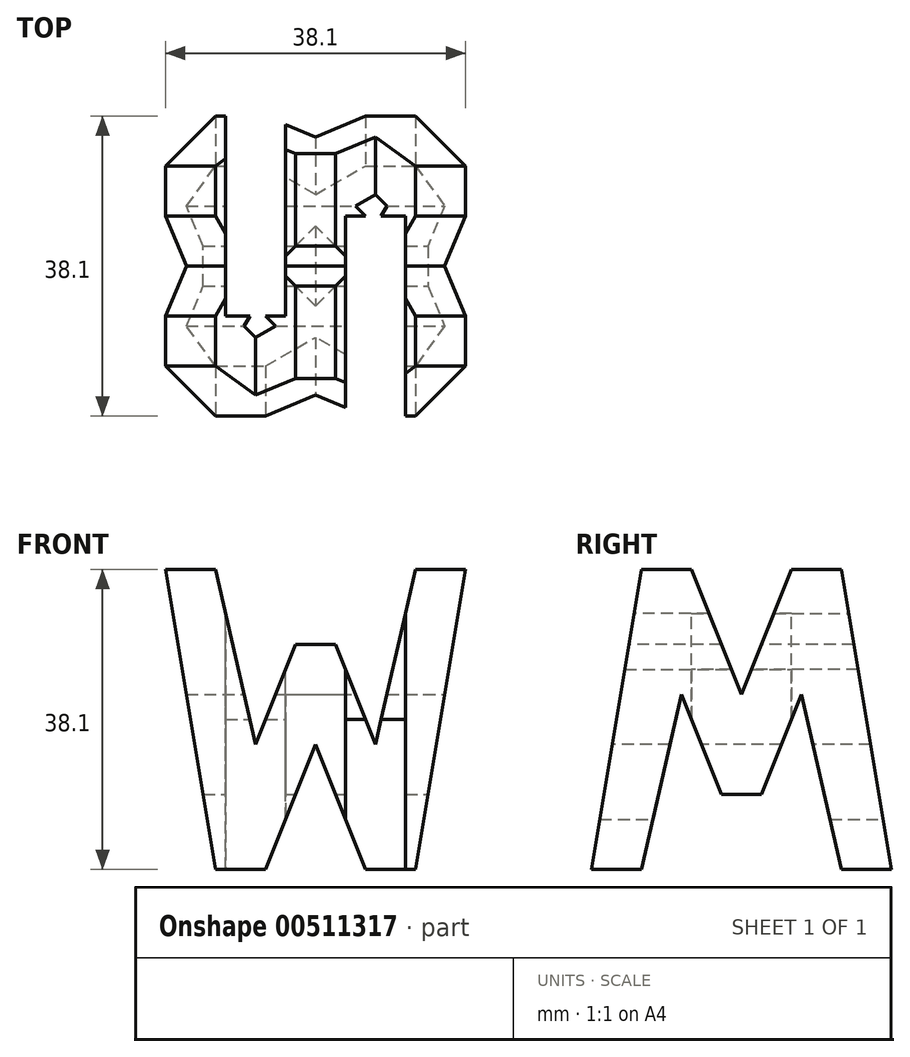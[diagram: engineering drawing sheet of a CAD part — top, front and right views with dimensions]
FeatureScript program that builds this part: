
annotation { "Feature Type Name" : "Feature", "Feature Type Description" : "" }
export const myFeature = defineFeature(function(context is Context, id is Id, definition is map)
    precondition{}
    {
        {
            var Q0;
            Q0=qCreatedBy(makeId("Front.planeOp"),FACE);
            var sketch = newSketch(context, id + "F0", { "sketchPlane" : qUnion([Q0])});
            skLineSegment(sketch, "E0", {"start": v(0, 0) * mm, "end": v(0, 38.1) * mm});
            skLineSegment(sketch, "E1", {"start": v(0, 38.1) * mm, "end": v(38.1, 38.1) * mm});
            skLineSegment(sketch, "E2", {"start": v(38.1, 38.1) * mm, "end": v(38.1, 0) * mm});
            skLineSegment(sketch, "E3", {"start": v(38.1, 0) * mm, "end": v(0, 0) * mm});
            skSolve(sketch);
        }
        {
            var Q0;
            Q0=makeQuery(id+"F0.imprint","IMPRINT",FACE,{"disambiguationData":[TD([[makeQuery(id+"F0.imprint","IMPRINT",EDGE,{"derivedFrom":sQuery(id+"F0.wireOp",EDGE,"E0")}),-1.0]])]});
            extrude(context, id + "F1", {"entities" : qUnion([Q0]), "depth" : 38.1 * mm, "offsetDistance" : 25.4 * mm});
        }
        {
            var Q0;
            Q0=qCreatedBy(makeId("Front.planeOp"),FACE);
            var Q1;
            Q1 = qBodyType(qCreatedBy(id + "F5" ,EDGE), BodyType.WIRE);
            cPlane(context, id + "F2", {"entities" : qUnion([Q0, Q1]), "cplaneType" : CPlaneType.OFFSET, "offset" : 38.1 * mm, "width" : 152.4 * mm, "height" : 152.4 * mm});
        }
        {
            var Q0;
            Q0=qCreatedBy(makeId("Right.planeOp"),FACE);
            cPlane(context, id + "F3", {"entities" : qUnion([Q0]), "cplaneType" : CPlaneType.OFFSET, "offset" : 38.1 * mm, "width" : 152.4 * mm, "height" : 152.4 * mm});
        }
        {
            var Q0;
            Q0=qCreatedBy(makeId("Top.planeOp"),FACE);
            cPlane(context, id + "F4", {"entities" : qUnion([Q0]), "cplaneType" : CPlaneType.OFFSET, "offset" : 38.1 * mm, "width" : 152.4 * mm, "height" : 152.4 * mm});
        }
        {
            var Q0;
            Q0=qCreatedBy(id+"F2.planeOp",FACE);
            var sketch = newSketch(context, id + "F5", { "sketchPlane" : qUnion([Q0])});
            skLineSegment(sketch, "E4.bottom", {"start": v(0, 0) * mm, "end": v(38.1, 0) * mm});
            skLineSegment(sketch, "E4.top", {"start": v(0, 38.1) * mm, "end": v(38.1, 38.1) * mm});
            skLineSegment(sketch, "E4.left", {"start": v(0, 0) * mm, "end": v(0, 38.1) * mm});
            skLineSegment(sketch, "E4.right", {"start": v(38.1, 0) * mm, "end": v(38.1, 38.1) * mm});
            skLineSegment(sketch, "E5", {"start": v(0, 38.1) * mm, "end": v(6.35, 0) * mm});
            skLineSegment(sketch, "E6", {"start": v(19.05, 15.87) * mm, "end": v(12.7, 0) * mm});
            skLineSegment(sketch, "E7", {"start": v(19.05, 15.87) * mm, "end": v(25.4, 0) * mm});
            skLineSegment(sketch, "E8", {"start": v(31.75, 0) * mm, "end": v(38.1, 38.1) * mm});
            skLineSegment(sketch, "E9", {"start": v(6.35, 38.1) * mm, "end": v(11.43, 15.87) * mm});
            skLineSegment(sketch, "E10", {"start": v(11.43, 15.87) * mm, "end": v(16.51, 28.57) * mm});
            skLineSegment(sketch, "E11", {"start": v(16.51, 28.57) * mm, "end": v(21.6, 28.57) * mm});
            skLineSegment(sketch, "E12", {"start": v(21.6, 28.57) * mm, "end": v(26.67, 15.87) * mm});
            skLineSegment(sketch, "E13", {"start": v(26.67, 15.87) * mm, "end": v(31.75, 38.1) * mm});
            skSolve(sketch);
        }
        {
            var Q0;
            {var subQ0=sQuery(id+"F5.wireOp",EDGE,"E6");Q0=makeQuery(id+"F5.imprint","IMPRINT",FACE,{"disambiguationData":[TD([[makeQuery(id+"F5.imprint","IMPRINT",EDGE,{"derivedFrom":subQ0}),1.0]])]});}
            var Q1;
            {var subQ0=sQuery(id+"F5.wireOp",EDGE,"E4.left");Q1=makeQuery(id+"F5.imprint","IMPRINT",FACE,{"disambiguationData":[TD([[makeQuery(id+"F5.imprint","IMPRINT",EDGE,{"derivedFrom":subQ0}),-1.0]])]});}
            var Q2;
            {var subQ0=sQuery(id+"F5.wireOp",EDGE,"E4.right");Q2=makeQuery(id+"F5.imprint","IMPRINT",FACE,{"disambiguationData":[TD([[makeQuery(id+"F5.imprint","IMPRINT",EDGE,{"derivedFrom":subQ0}),1.0]])]});}
            var Q3;
            {var subQ0=sQuery(id+"F5.wireOp",EDGE,"E9");Q3=makeQuery(id+"F5.imprint","IMPRINT",FACE,{"disambiguationData":[TD([[makeQuery(id+"F5.imprint","IMPRINT",EDGE,{"derivedFrom":subQ0}),1.0]])]});}
            extrude(context, id + "F6", {"entities" : qUnion([Q0, Q1, Q2, Q3]), "operationType" : NewBodyOperationType.REMOVE, "oppositeDirection" : true, "depth" : 38.1 * mm, "offsetDistance" : 25.4 * mm});
        }
        {
            var Q0;
            Q0=qCreatedBy(id+"F3.planeOp",FACE);
            var sketch = newSketch(context, id + "F7", { "sketchPlane" : qUnion([Q0])});
            skLineSegment(sketch, "E14", {"start": v(-31.75, 38.1) * mm, "end": v(-38.1, 0) * mm});
            skLineSegment(sketch, "E15", {"start": v(-25.4, 38.1) * mm, "end": v(-19.05, 22.23) * mm});
            skLineSegment(sketch, "E16", {"start": v(-19.05, 22.22) * mm, "end": v(-12.7, 38.1) * mm});
            skLineSegment(sketch, "E17", {"start": v(-6.35, 38.1) * mm, "end": v(0, 0) * mm});
            skLineSegment(sketch, "E18", {"start": v(-6.35, 0) * mm, "end": v(-11.43, 22.23) * mm});
            skLineSegment(sketch, "E19", {"start": v(-11.43, 22.23) * mm, "end": v(-16.5, 9.53) * mm});
            skLineSegment(sketch, "E20", {"start": v(-16.5, 9.53) * mm, "end": v(-21.59, 9.53) * mm});
            skLineSegment(sketch, "E21", {"start": v(-21.59, 9.52) * mm, "end": v(-26.67, 22.23) * mm});
            skLineSegment(sketch, "E22", {"start": v(-26.67, 22.23) * mm, "end": v(-31.75, 0) * mm});
            skLineSegment(sketch, "E23.bottom", {"start": v(-38.1, 0) * mm, "end": v(0, 0) * mm});
            skLineSegment(sketch, "E23.top", {"start": v(-38.1, 38.1) * mm, "end": v(0, 38.1) * mm});
            skLineSegment(sketch, "E23.left", {"start": v(-38.1, 0) * mm, "end": v(-38.1, 38.1) * mm});
            skLineSegment(sketch, "E23.right", {"start": v(0, 0) * mm, "end": v(0, 38.1) * mm});
            skSolve(sketch);
        }
        {
            var Q0;
            {var subQ0=sQuery(id+"F7.wireOp",EDGE,"E14");Q0=makeQuery(id+"F7.imprint","IMPRINT",FACE,{"disambiguationData":[TD([[makeQuery(id+"F7.imprint","IMPRINT",EDGE,{"derivedFrom":subQ0}),-1.0]])]});}
            var Q1;
            {var subQ0=sQuery(id+"F7.wireOp",EDGE,"E15");Q1=makeQuery(id+"F7.imprint","IMPRINT",FACE,{"disambiguationData":[TD([[makeQuery(id+"F7.imprint","IMPRINT",EDGE,{"derivedFrom":subQ0}),1.0]])]});}
            var Q2;
            {var subQ0=sQuery(id+"F7.wireOp",EDGE,"E17");Q2=makeQuery(id+"F7.imprint","IMPRINT",FACE,{"disambiguationData":[TD([[makeQuery(id+"F7.imprint","IMPRINT",EDGE,{"derivedFrom":subQ0}),1.0]])]});}
            var Q3;
            {var subQ0=sQuery(id+"F7.wireOp",EDGE,"E18");Q3=makeQuery(id+"F7.imprint","IMPRINT",FACE,{"disambiguationData":[TD([[makeQuery(id+"F7.imprint","IMPRINT",EDGE,{"derivedFrom":subQ0}),1.0]])]});}
            extrude(context, id + "F8", {"entities" : qUnion([Q0, Q1, Q2, Q3]), "operationType" : NewBodyOperationType.REMOVE, "oppositeDirection" : true, "depth" : 38.1 * mm, "offsetDistance" : 25.4 * mm});
        }
        {
            var Q0;
            Q0=qCreatedBy(id+"F4.planeOp",FACE);
            var sketch = newSketch(context, id + "F9", { "sketchPlane" : qUnion([Q0])});
            skLineSegment(sketch, "E24.bottom", {"start": v(0, -38.1) * mm, "end": v(38.1, -38.1) * mm});
            skLineSegment(sketch, "E24.top", {"start": v(0, 0) * mm, "end": v(38.1, 0) * mm});
            skLineSegment(sketch, "E24.left", {"start": v(0, -38.1) * mm, "end": v(0, 0) * mm});
            skLineSegment(sketch, "E24.right", {"start": v(38.1, -38.1) * mm, "end": v(38.1, 0) * mm});
            skLineSegment(sketch, "E25", {"start": v(7.62, 0) * mm, "end": v(7.62, -25.4) * mm});
            skLineSegment(sketch, "E26", {"start": v(7.62, -25.4) * mm, "end": v(15.24, -25.4) * mm});
            skLineSegment(sketch, "E27", {"start": v(15.24, -25.4) * mm, "end": v(15.24, 0) * mm});
            skLineSegment(sketch, "E28", {"start": v(30.48, -38.1) * mm, "end": v(30.48, -12.7) * mm});
            skLineSegment(sketch, "E29", {"start": v(30.48, -12.7) * mm, "end": v(22.86, -12.7) * mm});
            skLineSegment(sketch, "E30", {"start": v(22.86, -12.7) * mm, "end": v(22.86, -38.1) * mm});
            skSolve(sketch);
        }
        {
            var Q0;
            {var subQ0=sQuery(id+"F9.wireOp",EDGE,"E25");Q0=makeQuery(id+"F9.imprint","IMPRINT",FACE,{"disambiguationData":[TD([[makeQuery(id+"F9.imprint","IMPRINT",EDGE,{"derivedFrom":subQ0}),1.0]])]});}
            var Q1;
            {var subQ0=sQuery(id+"F9.wireOp",EDGE,"E28");Q1=makeQuery(id+"F9.imprint","IMPRINT",FACE,{"disambiguationData":[TD([[makeQuery(id+"F9.imprint","IMPRINT",EDGE,{"derivedFrom":subQ0}),1.0]])]});}
            extrude(context, id + "F10", {"entities" : qUnion([Q0, Q1]), "operationType" : NewBodyOperationType.REMOVE, "oppositeDirection" : true, "depth" : 38.1 * mm, "offsetDistance" : 25.4 * mm});
        }
    });
